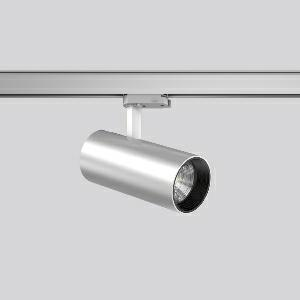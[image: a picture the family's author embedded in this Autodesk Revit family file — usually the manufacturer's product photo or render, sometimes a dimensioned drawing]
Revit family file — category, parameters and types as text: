
# Revit family: deecos_s_mini_742200_004_1_76_36ef
name_source: partatom
category: Lighting Fixtures
units: mm (PartAtom-declared; Revit-internal decimal feet)

## family parameters
Cut with Voids When Loaded = No
Host = Face
Light Source = No
Part Type = Normal
Room Calculation Point = No
Round Connector Dimension = Use Diameter
Shared = No

## types (1)
- DEECOS S mini (1 x LED Modul 940, 2150 lm, 4000)
    Apparent Load = 20 VA
    Approval mark = CE
    CIE Flux Codes = 98 100 100 100 100
    Color Rendering = 92
    Color Temperature = 4000
    Default Elevation = 1800 mm
    Description = Series: DEECOS S mini
LED surface-mounted projector in modern design with no visible cooling ribs. Housing: die-cast aluminium, powder-coated. Rotation range: 356°. Swivel range: 90°. Black plastic ring and recessed LED to prevent glare from the side. Optical assembly with lens made of plastic (polycarbonate) for the best homogeneous light distribution - can be changed without tools. Best colour rendering index Ra>90. With adapter for RZB 3-circuit DALI tracks. Suitable for Track on ceiling, Wall track. High quality converter without flickering and stroboscopic effect. The following accessories can be mounted without use of tools: interchangeable lenses, decorative glasses, honeycomb louvre, clear and frosted diffusers, white interchangeable plastic ring. 
Colour: silver
Diameter: 87 mm
Height: 214 mm
Lamp: LED
Socket: without socket
Colour temperature: 4000K
Colour rendering index (CRI): 92
System power: 20 W
Rated luminous flux: 2150 lm
Luminous efficiency: 108 lm/W
Control gear: Converter, dimmable, DALI
Protection class: I
Type of protection: IP 20
    Height = 214 mm
    Lamp = 1 x LED Modul 940
    Lamp Light Flux = 2150 lm
    Lamp count = 1
    Length = 87 mm
    Lifetime = 50000 h
    Luminous efficacy = 108 lm/W
    Manufacturer = RZB
    ModVariant = No
    Model = 742200.004.1.76
    Mounting Place = Ceiling
    Mounting Type = Rail mounted
    Number of Poles = 1
    OnlyDefault = Yes
    Power Factor = 1
    Product Name = DEECOS S mini
    Product group = Track mounted projectors
    ProductGroupID = 301
    Protection Class = Protection class I
    Protection Degree = IP 20
    RLX_Detail_Level = 1
    RLX_Emergency_Light_Flux = 0 lm
    RLX_Emergency_Type = 0
    RLX_Emergency_Type_DB = No
    RlxData = <blob elided: 37245 chars, md5=021aa3fc>
    Socket = socket
    Standby Power = 0 W
    System Light Flux = 2150 lm
    System Power = 20 W
    Type Comments = Product without accessories
    Type Image = 741930.004.jpg
    URL = http://relux.com
    VarID = ---
    Voltage = 230 V
    Voltage Range = 220-240 V
    Weight = 0.00 kg
    Width = 0 mm  [stored 0 ft]

note: [stored X ft] marks values corroborated as IEEE doubles in the binary element streams (Revit-internal decimal feet)

## geometry (parser evidence)
native form markers: Blend x4, Sweep x13
no freeform markers — native parametric forms only
